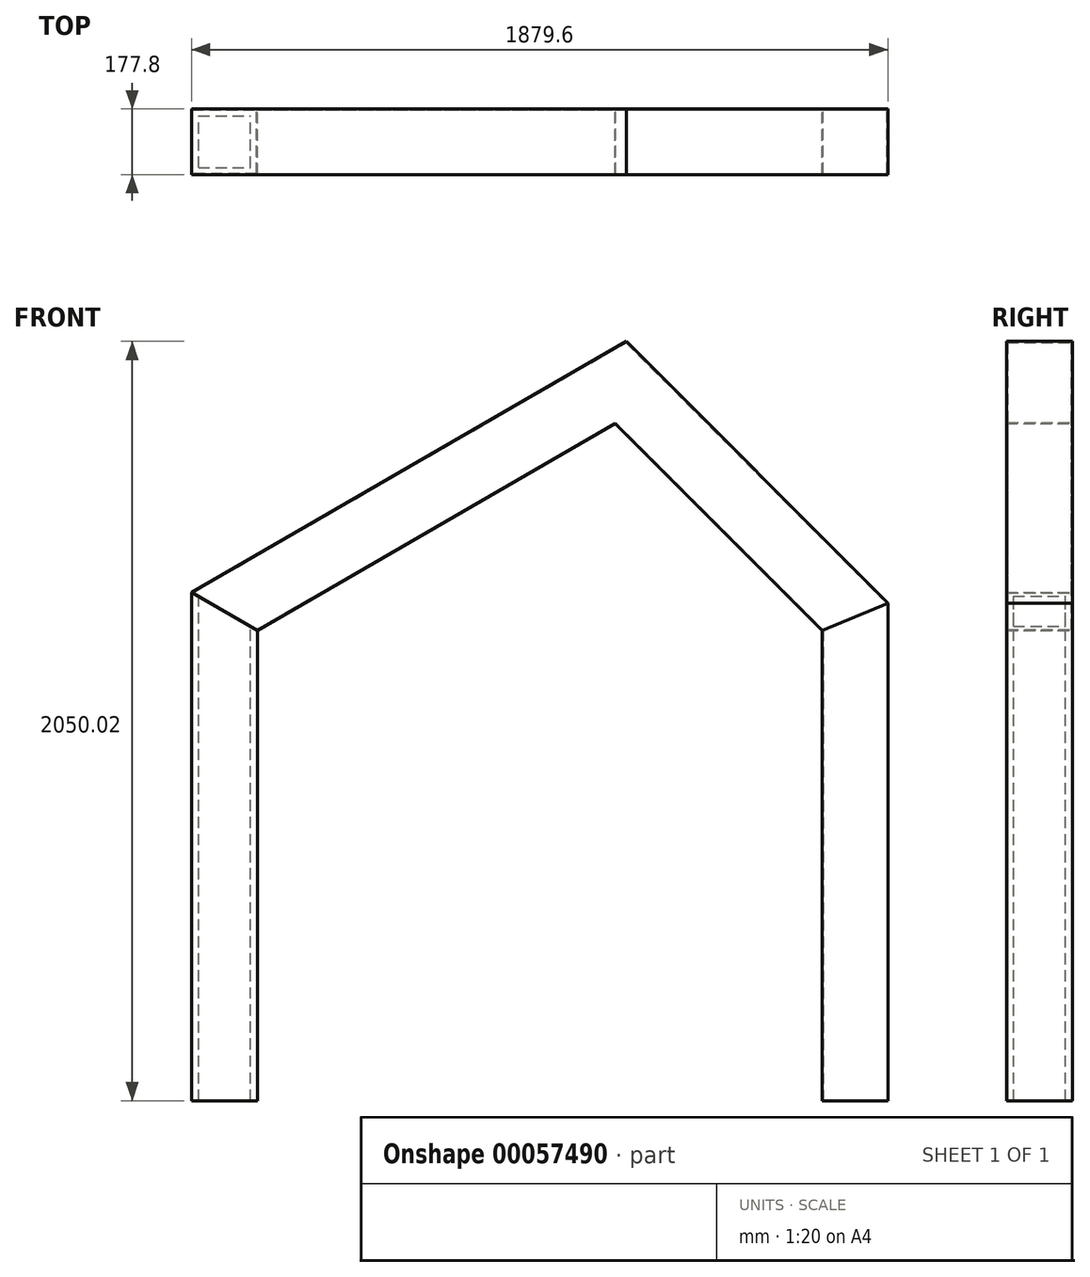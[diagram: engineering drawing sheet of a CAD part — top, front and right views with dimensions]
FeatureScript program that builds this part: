
annotation { "Feature Type Name" : "Feature", "Feature Type Description" : "" }
export const myFeature = defineFeature(function(context is Context, id is Id, definition is map)
    precondition{}
    {
        {
            var Q0;
            Q0=qCreatedBy(makeId("Front.planeOp"),FACE);
            var sketch = newSketch(context, id + "F0", { "sketchPlane" : qUnion([Q0])});
            skLineSegment(sketch, "E0", {"start": v(-966.18, 0) * mm, "end": v(-966.18, 1270) * mm});
            skLineSegment(sketch, "E1", {"start": v(-966.18, 1270) * mm, "end": v(0, 1827.82) * mm});
            skLineSegment(sketch, "E2", {"start": v(0, 1827.82) * mm, "end": v(557.82, 1270) * mm});
            skLineSegment(sketch, "E3", {"start": v(557.82, 1270) * mm, "end": v(557.82, 0) * mm});
            skLineSegment(sketch, "E4.0", {"start": v(735.62, 1343.65) * mm, "end": v(735.62, 0) * mm});
            skLineSegment(sketch, "E4.1", {"start": v(29.25, 2050.02) * mm, "end": v(735.62, 1343.65) * mm});
            skLineSegment(sketch, "E4.2", {"start": v(-1143.98, 1372.65) * mm, "end": v(29.25, 2050.02) * mm});
            skLineSegment(sketch, "E4.3", {"start": v(-1143.98, 0) * mm, "end": v(-1143.98, 1372.65) * mm});
            skLineSegment(sketch, "E5", {"start": v(-966.18, 1270) * mm, "end": v(-1143.98, 1372.65) * mm});
            skLineSegment(sketch, "E6", {"start": v(557.82, 1270) * mm, "end": v(735.62, 1343.65) * mm});
            skLineSegment(sketch, "E7", {"start": v(-1143.98, 0) * mm, "end": v(-966.18, 0) * mm});
            skLineSegment(sketch, "E8", {"start": v(557.82, 0) * mm, "end": v(735.62, 0) * mm});
            skSolve(sketch);
        }
        {
            var Q0;
            Q0=makeQuery(id+"F0.imprint","IMPRINT",FACE,{"disambiguationData":[TD([[makeQuery(id+"F0.imprint","IMPRINT",EDGE,{"derivedFrom":sQuery(id+"F0.wireOp",EDGE,"E1")}),1.0]])]});
            extrude(context, id + "F1", {"entities" : qUnion([Q0]), "endBound" : BoundingType.SYMMETRIC, "depth" : 177.8 * mm});
        }
        {
            var Q0;
            Q0=makeQuery(id+"F0.imprint","IMPRINT",FACE,{"disambiguationData":[TD([[makeQuery(id+"F0.imprint","IMPRINT",EDGE,{"derivedFrom":sQuery(id+"F0.wireOp",EDGE,"E0")}),1.0]])]});
            extrude(context, id + "F2", {"entities" : qUnion([Q0]), "endBound" : BoundingType.SYMMETRIC, "depth" : 177.8 * mm});
        }
        {
            var Q0;
            Q0=makeQuery(id+"F0.imprint","IMPRINT",FACE,{"disambiguationData":[TD([[makeQuery(id+"F0.imprint","IMPRINT",EDGE,{"derivedFrom":sQuery(id+"F0.wireOp",EDGE,"E3")}),1.0]])]});
            extrude(context, id + "F3", {"entities" : qUnion([Q0]), "endBound" : BoundingType.SYMMETRIC, "depth" : 177.8 * mm});
        }
        {
            var Q0;
            Q0=makeQuery(id+"F2.opExtrude","SWEPT_FACE",FACE,{"disambiguationData":[OSD([sQuery(id+"F0.wireOp",EDGE,"E5")])]});
            var Q1;
            Q1=makeQuery(id+"F2.opExtrude","SWEPT_FACE",FACE,{"disambiguationData":[OSD([sQuery(id+"F0.wireOp",EDGE,"E7")])]});
            shell(context, id + "F4", {"entities" : qUnion([Q0, Q1]), "thickness" : 19.05 * mm});
        }
        {
            var Q0;
            Q0=makeQuery(id+"F3.opExtrude","SWEPT_FACE",FACE,{"disambiguationData":[OSD([sQuery(id+"F0.wireOp",EDGE,"E6")])]});
            var Q1;
            Q1=makeQuery(id+"F3.opExtrude","SWEPT_FACE",FACE,{"disambiguationData":[OSD([sQuery(id+"F0.wireOp",EDGE,"E8")])]});
            shell(context, id + "F5", {"entities" : qUnion([Q0, Q1]), "thickness" : 2.54 * mm});
        }
        {
            var Q0;
            Q0=makeQuery(id+"F1.opExtrude","SWEPT_FACE",FACE,{"disambiguationData":[OSD([sQuery(id+"F0.wireOp",EDGE,"E5")])]});
            var Q1;
            Q1=makeQuery(id+"F1.opExtrude","SWEPT_FACE",FACE,{"disambiguationData":[OSD([sQuery(id+"F0.wireOp",EDGE,"E6")])]});
            shell(context, id + "F6", {"entities" : qUnion([Q0, Q1]), "thickness" : 2.54 * mm});
        }
    });
